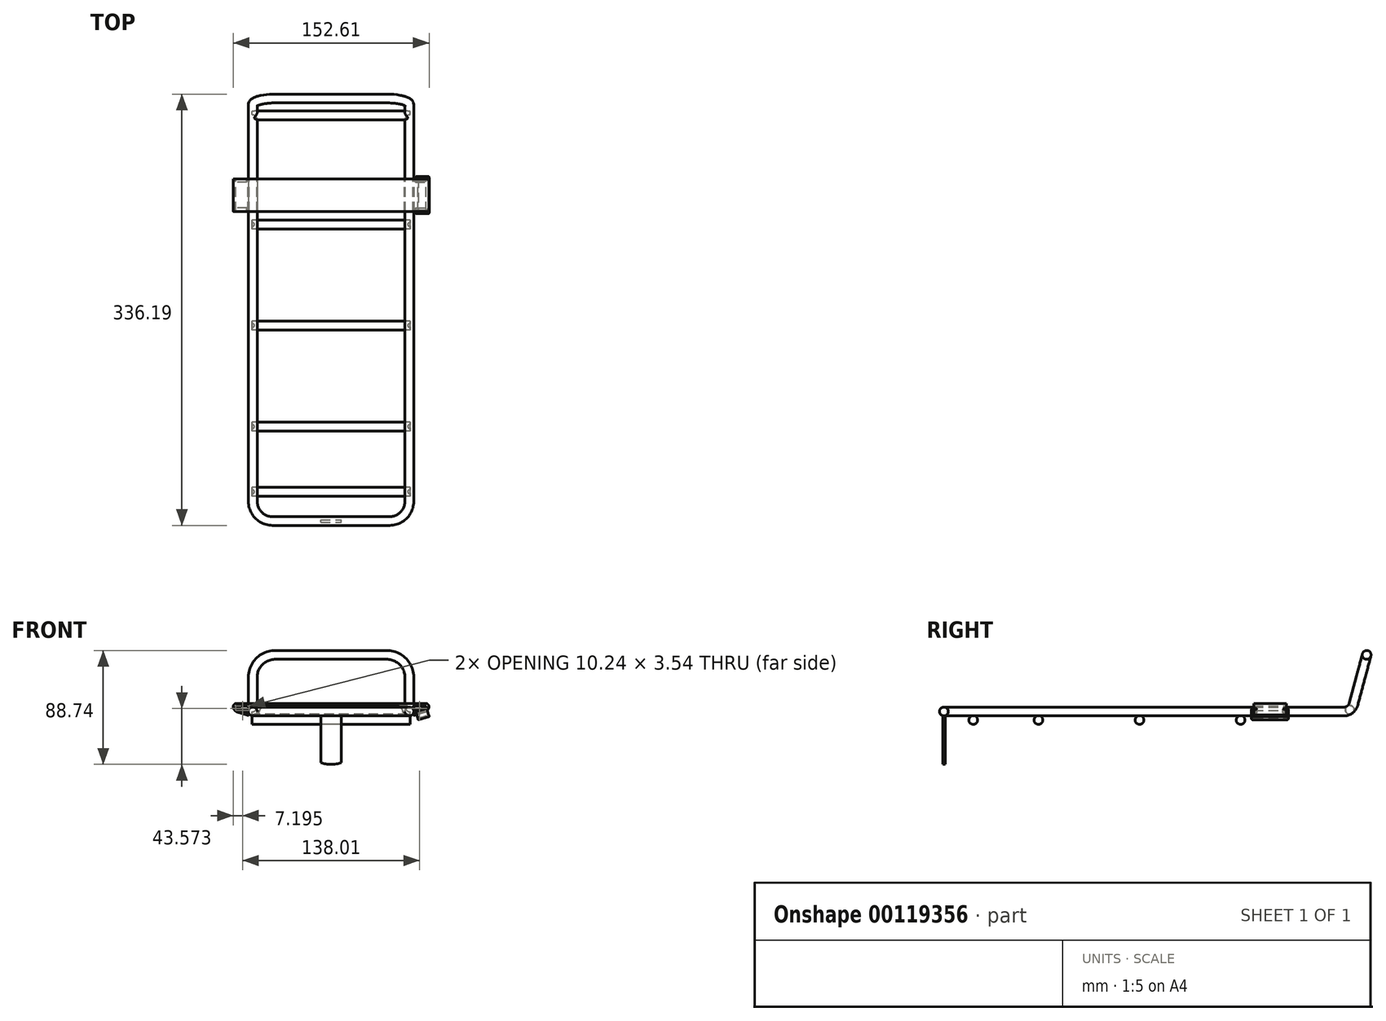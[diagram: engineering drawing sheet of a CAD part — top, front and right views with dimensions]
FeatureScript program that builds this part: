
annotation { "Feature Type Name" : "Feature", "Feature Type Description" : "" }
export const myFeature = defineFeature(function(context is Context, id is Id, definition is map)
    precondition{}
    {
        {
            var Q0;
            Q0=qCreatedBy(makeId("Right.planeOp"),FACE);
            var sketch = newSketch(context, id + "F0", { "sketchPlane" : qUnion([Q0])});
            skCircle(sketch, "E0", {"center": v(0, 0) * mm, "radius": 3.43 * mm});
            skSolve(sketch);
        }
        {
            var Q0;
            Q0=qCreatedBy(makeId("Top.planeOp"),FACE);
            var sketch = newSketch(context, id + "F1", { "sketchPlane" : qUnion([Q0])});
            skLineSegment(sketch, "E1", {"start": v(0, 0) * mm, "end": v(45.72, 0) * mm});
            skArc(sketch, "E2", {"start": v(45.72, 0) * mm, "mid": v(56.5, 4.46) * mm, "end": v(60.96, 15.24) * mm});
            skLineSegment(sketch, "E3", {"start": v(45.72, 0) * mm, "end": v(60.96, 0) * mm, "construction": true});
            skLineSegment(sketch, "E4", {"start": v(60.96, 0) * mm, "end": v(60.96, 15.24) * mm, "construction": true});
            skSolve(sketch);
        }
        {
            var Q0;
            Q0=sQuery(id+"F1.wireOp",EDGE,"E4");
            cPlane(context, id + "F2", {"entities" : qUnion([Q0]), "cplaneType" : CPlaneType.LINE_ANGLE, "offset" : 25.4 * mm, "angle" : 90 * degree, "width" : 152.4 * mm, "height" : 152.4 * mm});
        }
        {
            var Q0;
            Q0=qCreatedBy(id+"F2.planeOp",FACE);
            var sketch = newSketch(context, id + "F3", { "sketchPlane" : qUnion([Q0])});
            skLineSegment(sketch, "E5", {"start": v(15.24, 0) * mm, "end": v(311.65, 0) * mm});
            skArc(sketch, "E6", {"start": v(311.65, 0) * mm, "mid": v(316.3, 1.57) * mm, "end": v(319.01, 5.65) * mm});
            skLineSegment(sketch, "E7", {"start": v(311.65, 0) * mm, "end": v(317.5, 0) * mm, "construction": true});
            skLineSegment(sketch, "E8", {"start": v(317.5, 0) * mm, "end": v(319.01, 5.65) * mm, "construction": true});
            skSolve(sketch);
        }
        {
            var Q0;
            Q0=sQuery(id+"F3.wireOp",EDGE,"E8");
            cPlane(context, id + "F4", {"entities" : qUnion([Q0]), "cplaneType" : CPlaneType.LINE_ANGLE, "offset" : 25.4 * mm, "angle" : 90 * degree, "width" : 152.4 * mm, "height" : 152.4 * mm});
        }
        {
            var Q0;
            Q0=qCreatedBy(id+"F4.planeOp",FACE);
            var sketch = newSketch(context, id + "F5", { "sketchPlane" : qUnion([Q0])});
            skLineSegment(sketch, "E9", {"start": v(-60.96, 88.02) * mm, "end": v(-60.96, 110.12) * mm});
            skArc(sketch, "E10", {"start": v(-43.18, 127.9) * mm, "mid": v(-55.75, 122.69) * mm, "end": v(-60.96, 110.12) * mm});
            skLineSegment(sketch, "E11", {"start": v(-43.18, 127.9) * mm, "end": v(43.18, 127.9) * mm});
            skArc(sketch, "E12", {"start": v(60.96, 110.12) * mm, "mid": v(55.75, 122.69) * mm, "end": v(43.18, 127.9) * mm});
            skLineSegment(sketch, "E13", {"start": v(60.96, 110.12) * mm, "end": v(60.96, 88.02) * mm});
            skLineSegment(sketch, "E14", {"start": v(-60.96, 110.12) * mm, "end": v(-60.96, 127.9) * mm, "construction": true});
            skLineSegment(sketch, "E15", {"start": v(-60.96, 127.9) * mm, "end": v(-43.18, 127.9) * mm, "construction": true});
            skLineSegment(sketch, "E16", {"start": v(43.18, 127.9) * mm, "end": v(60.96, 127.9) * mm, "construction": true});
            skLineSegment(sketch, "E17", {"start": v(60.96, 127.9) * mm, "end": v(60.96, 110.12) * mm, "construction": true});
            skLineSegment(sketch, "E18", {"start": v(-60.96, 88.02) * mm, "end": v(60.96, 88.02) * mm, "construction": true});
            skLineSegment(sketch, "E19", {"start": v(0, 88.02) * mm, "end": v(0, 0) * mm, "construction": true});
            skSolve(sketch);
        }
        {
            var Q0;
            Q0=sQuery(id+"F5.wireOp",EDGE,"E13");
            cPlane(context, id + "F6", {"entities" : qUnion([Q0]), "cplaneType" : CPlaneType.LINE_ANGLE, "offset" : 25.4 * mm, "angle" : 0 * degree, "width" : 152.4 * mm, "height" : 152.4 * mm});
        }
        {
            var Q0;
            Q0=qCreatedBy(id+"F6.planeOp",FACE);
            var sketch = newSketch(context, id + "F7", { "sketchPlane" : qUnion([Q0])});
            skArc(sketch, "E20", {"start": v(-319.01, 5.65) * mm, "mid": v(-316.3, 1.57) * mm, "end": v(-311.65, 0) * mm});
            skLineSegment(sketch, "E21", {"start": v(-311.65, 0) * mm, "end": v(-15.24, 0) * mm});
            skSolve(sketch);
        }
        {
            var Q0;
            Q0=qCreatedBy(makeId("Top.planeOp"),FACE);
            var sketch = newSketch(context, id + "F8", { "sketchPlane" : qUnion([Q0])});
            skArc(sketch, "E22", {"start": v(-60.96, 15.24) * mm, "mid": v(-56.5, 4.46) * mm, "end": v(-45.72, 0) * mm});
            skLineSegment(sketch, "E23", {"start": v(-45.72, 0) * mm, "end": v(0, 0) * mm});
            skSolve(sketch);
        }
        {
            var Q0;
            Q0=qSketchRegion(id+"F0",true);
            var Q1;
            Q1=qConstructionFilter(qBodyType(qCreatedBy(id+"F1",EDGE),BodyType.WIRE),ConstructionObject.NO);
            var Q2;
            Q2=qConstructionFilter(qBodyType(qCreatedBy(id+"F3",EDGE),BodyType.WIRE),ConstructionObject.NO);
            var Q3;
            Q3=qConstructionFilter(qBodyType(qCreatedBy(id+"F5",EDGE),BodyType.WIRE),ConstructionObject.NO);
            var Q4;
            Q4=qConstructionFilter(qBodyType(qCreatedBy(id+"F7",EDGE),BodyType.WIRE),ConstructionObject.NO);
            var Q5;
            Q5=qConstructionFilter(qBodyType(qCreatedBy(id+"F8",EDGE),BodyType.WIRE),ConstructionObject.NO);
            sweep(context, id + "F9", {"profiles" : qUnion([Q0]), "path" : qUnion([Q1, Q2, Q3, Q4, Q5])});
        }
        {
            var Q0;
            Q0=qCreatedBy(makeId("Front.planeOp"),FACE);
            var sketch = newSketch(context, id + "F10", { "sketchPlane" : qUnion([Q0])});
            skLineSegment(sketch, "E24.bottom", {"start": v(-8, 0) * mm, "end": v(8, 0) * mm});
            skLineSegment(sketch, "E24.left", {"start": v(-8, 0) * mm, "end": v(-8, -39.85) * mm});
            skLineSegment(sketch, "E24.right", {"start": v(8, 0) * mm, "end": v(8, -39.85) * mm});
            skArc(sketch, "E25", {"start": v(-8, -39.85) * mm, "mid": v(0, -41.15) * mm, "end": v(8, -39.85) * mm});
            skSolve(sketch);
        }
        {
            var Q0;
            Q0=qSketchRegion(id+"F10",true);
            extrude(context, id + "F11", {"entities" : qUnion([Q0]), "operationType" : NewBodyOperationType.ADD, "endBound" : BoundingType.SYMMETRIC, "depth" : 2.03 * mm});
        }
        {
            var Q0;
            Q0=qCreatedBy(makeId("Right.planeOp"),FACE);
            var sketch = newSketch(context, id + "F12", { "sketchPlane" : qUnion([Q0])});
            skCircle(sketch, "E26", {"center": v(22.86, -6.6) * mm, "radius": 3.43 * mm});
            skCircle(sketch, "E27", {"center": v(73.66, -6.6) * mm, "radius": 3.43 * mm});
            skLineSegment(sketch, "E28", {"start": v(0, -3.18) * mm, "end": v(311.65, -3.18) * mm, "construction": true});
            skCircle(sketch, "E29", {"center": v(152.4, -6.6) * mm, "radius": 3.43 * mm});
            skCircle(sketch, "E30", {"center": v(231.14, -6.6) * mm, "radius": 3.43 * mm});
            skCircle(sketch, "E31", {"center": v(316.23, 1.27) * mm, "radius": 3.43 * mm});
            skSolve(sketch);
        }
        {
            var Q0;
            Q0=qSketchRegion(id+"F12",true);
            extrude(context, id + "F13", {"entities" : qUnion([Q0]), "operationType" : NewBodyOperationType.ADD, "endBound" : BoundingType.SYMMETRIC, "depth" : 123.19 * mm});
        }
        {
            var Q0;
            Q0=qCreatedBy(makeId("Front.planeOp"),FACE);
            cPlane(context, id + "F14", {"entities" : qUnion([Q0]), "cplaneType" : CPlaneType.OFFSET, "offset" : 266.7 * mm, "oppositeDirection" : true, "width" : 152.4 * mm, "height" : 152.4 * mm});
        }
        {
            var Q0;
            Q0=qCreatedBy(id+"F14.planeOp",FACE);
            var sketch = newSketch(context, id + "F15", { "sketchPlane" : qUnion([Q0])});
            skCircle(sketch, "E32", {"center": v(-60.96, 0) * mm, "radius": 3.43 * mm, "construction": true});
            skCircle(sketch, "E33", {"center": v(60.96, 0) * mm, "radius": 3.43 * mm, "construction": true});
            skLineSegment(sketch, "E34", {"start": v(60.96, 3.43) * mm, "end": v(-60.96, 3.43) * mm, "construction": true});
            skArc(sketch, "E35", {"start": v(73.91, 6.22) * mm, "mid": v(75.53, 5.55) * mm, "end": v(76.2, 3.94) * mm});
            skArc(sketch, "E36", {"start": v(76.2, 3.94) * mm, "mid": v(75.3, 1.22) * mm, "end": v(72.96, -0.44) * mm});
            skArc(sketch, "E37", {"start": v(-73.91, 6.22) * mm, "mid": v(-75.53, 5.55) * mm, "end": v(-76.2, 3.94) * mm});
            skArc(sketch, "E38", {"start": v(-76.2, 3.94) * mm, "mid": v(-75.3, 1.22) * mm, "end": v(-72.96, -0.44) * mm});
            skArc(sketch, "E39", {"start": v(64.2, -2.2) * mm, "mid": v(60.96, 3.43) * mm, "end": v(57.72, -2.2) * mm});
            skArc(sketch, "E40", {"start": v(64.2, -2.2) * mm, "mid": v(64.25, -2.76) * mm, "end": v(64.8, -2.93) * mm});
            skArc(sketch, "E41", {"start": v(57.72, -2.2) * mm, "mid": v(57.54, -2.88) * mm, "end": v(56.85, -2.73) * mm});
            skArc(sketch, "E42", {"start": v(-57.72, -2.2) * mm, "mid": v(-60.96, 3.43) * mm, "end": v(-64.2, -2.2) * mm});
            skArc(sketch, "E43", {"start": v(-57.72, -2.2) * mm, "mid": v(-57.54, -2.88) * mm, "end": v(-56.85, -2.73) * mm});
            skLineSegment(sketch, "E44", {"start": v(-72.96, -0.44) * mm, "end": v(-64.8, -2.93) * mm});
            skArc(sketch, "E45", {"start": v(-64.2, -2.2) * mm, "mid": v(-64.25, -2.76) * mm, "end": v(-64.8, -2.93) * mm});
            skLineSegment(sketch, "E46", {"start": v(64.8, -2.93) * mm, "end": v(72.96, -0.44) * mm});
            skLineSegment(sketch, "E47", {"start": v(73.91, 6.22) * mm, "end": v(0, 6.22) * mm});
            skLineSegment(sketch, "E48", {"start": v(0, 6.22) * mm, "end": v(-73.91, 6.22) * mm});
            skLineSegment(sketch, "E49", {"start": v(50.99, 4.2) * mm, "end": v(-50.99, 4.2) * mm});
            skArc(sketch, "E50", {"start": v(-56.85, -2.73) * mm, "mid": v(-56.3, -1.63) * mm, "end": v(-56.05, -0.44) * mm});
            skArc(sketch, "E51", {"start": v(56.05, -0.44) * mm, "mid": v(56.3, -1.63) * mm, "end": v(56.85, -2.73) * mm});
            skArc(sketch, "E52", {"start": v(56.05, -0.44) * mm, "mid": v(54.42, 2.86) * mm, "end": v(50.99, 4.2) * mm});
            skArc(sketch, "E53", {"start": v(-50.99, 4.2) * mm, "mid": v(-54.42, 2.86) * mm, "end": v(-56.05, -0.44) * mm});
            skLineSegment(sketch, "E54", {"start": v(64.64, -2.45) * mm, "end": v(57.28, -2.45) * mm, "construction": true});
            skLineSegment(sketch, "E55", {"start": v(-57.28, -2.45) * mm, "end": v(-64.64, -2.45) * mm, "construction": true});
            skSolve(sketch);
        }
        {
            var Q0;
            Q0=qSketchRegion(id+"F15",true);
            extrude(context, id + "F16", {"entities" : qUnion([Q0]), "depth" : 25.4 * mm});
        }
        {
            var Q0;
            Q0=makeQuery(id+"F16.opExtrude","CAP_FACE",FACE,{"disambiguationData":[OSD([sQuery(id+"F15.wireOp",EDGE,"E35"),sQuery(id+"F15.wireOp",EDGE,"E36"),sQuery(id+"F15.wireOp",EDGE,"E37"),sQuery(id+"F15.wireOp",EDGE,"E38"),sQuery(id+"F15.wireOp",EDGE,"E39"),sQuery(id+"F15.wireOp",EDGE,"E40"),sQuery(id+"F15.wireOp",EDGE,"E41"),sQuery(id+"F15.wireOp",EDGE,"E42"),sQuery(id+"F15.wireOp",EDGE,"E43"),sQuery(id+"F15.wireOp",EDGE,"E44"),sQuery(id+"F15.wireOp",EDGE,"E45"),sQuery(id+"F15.wireOp",EDGE,"E46"),sQuery(id+"F15.wireOp",EDGE,"E47"),sQuery(id+"F15.wireOp",EDGE,"E48"),sQuery(id+"F15.wireOp",EDGE,"E49"),sQuery(id+"F15.wireOp",EDGE,"E50"),sQuery(id+"F15.wireOp",EDGE,"E51"),sQuery(id+"F15.wireOp",EDGE,"E52"),sQuery(id+"F15.wireOp",EDGE,"E53")])],"isStart":true});
            var sketch = newSketch(context, id + "F17", { "sketchPlane" : qUnion([Q0])});
            skLineSegment(sketch, "E56", {"start": v(62.5, 4.2) * mm, "end": v(73.51, 4.2) * mm});
            skLineSegment(sketch, "E57", {"start": v(65.65, 0.52) * mm, "end": v(73.7, 2.97) * mm});
            skArc(sketch, "E58", {"start": v(73.51, 4.2) * mm, "mid": v(74.13, 3.66) * mm, "end": v(73.7, 2.97) * mm});
            skArc(sketch, "E59", {"start": v(65.65, 0.52) * mm, "mid": v(64.57, 2.78) * mm, "end": v(62.5, 4.2) * mm});
            skLineSegment(sketch, "E60", {"start": v(-73.51, 4.2) * mm, "end": v(-62.5, 4.2) * mm});
            skLineSegment(sketch, "E61", {"start": v(-65.65, 0.52) * mm, "end": v(-73.7, 2.97) * mm});
            skArc(sketch, "E62", {"start": v(-73.51, 4.2) * mm, "mid": v(-74.13, 3.66) * mm, "end": v(-73.7, 2.97) * mm});
            skArc(sketch, "E63", {"start": v(-62.5, 4.2) * mm, "mid": v(-64.57, 2.78) * mm, "end": v(-65.65, 0.52) * mm});
            skSolve(sketch);
        }
        {
            var Q0;
            Q0=qSketchRegion(id+"F17",true);
            extrude(context, id + "F18", {"entities" : qUnion([Q0]), "operationType" : NewBodyOperationType.REMOVE, "endBound" : BoundingType.UP_TO_NEXT, "oppositeDirection" : true, "depth" : 25.4 * mm});
        }
        {
            var Q0;
            Q0=makeQuery(id+"F16.opExtrude","SWEPT_EDGE",EDGE,{"disambiguationData":[OSD([sQuery(id+"F15.wireOp",EDGE,"E36"),sQuery(id+"F15.wireOp",EDGE,"E46")])]});
            var Q1;
            Q1=makeQuery(id+"F16.opExtrude","SWEPT_FACE",FACE,{"disambiguationData":[OSD([sQuery(id+"F15.wireOp",EDGE,"E46")])]});
            cPlane(context, id + "F19", {"entities" : qUnion([Q0, Q1]), "cplaneType" : CPlaneType.LINE_ANGLE, "offset" : 25.4 * mm, "angle" : 90 * degree, "width" : 152.4 * mm, "height" : 152.4 * mm});
        }
        {
            var Q0;
            Q0=qCreatedBy(id+"F19.planeOp",FACE);
            var sketch = newSketch(context, id + "F20", { "sketchPlane" : qUnion([Q0])});
            skLineSegment(sketch, "E64", {"start": v(241.3, -20.93) * mm, "end": v(241.3, -19.5) * mm});
            skLineSegment(sketch, "E65", {"start": v(241.3, -19.5) * mm, "end": v(243.95, -20.22) * mm});
            skLineSegment(sketch, "E66", {"start": v(243.95, -20.22) * mm, "end": v(241.3, -20.93) * mm});
            skLineSegment(sketch, "E67", {"start": v(241.3, -21.74) * mm, "end": v(241.3, -20.93) * mm, "construction": true});
            skLineSegment(sketch, "E68", {"start": v(266.7, -21.74) * mm, "end": v(266.7, -20.93) * mm, "construction": true});
            skLineSegment(sketch, "E69", {"start": v(266.7, -20.93) * mm, "end": v(266.7, -19.5) * mm});
            skLineSegment(sketch, "E70", {"start": v(266.7, -19.5) * mm, "end": v(264.05, -20.22) * mm});
            skLineSegment(sketch, "E71", {"start": v(264.05, -20.22) * mm, "end": v(266.7, -20.93) * mm});
            skSolve(sketch);
        }
        {
            var Q0;
            Q0=qSketchRegion(id+"F20",true);
            var Q1;
            Q1=makeQuery(id+"F18.boolean.opBoolean","COPY",FACE,{"derivedFrom":makeQuery(id+"F18.opExtrude","SWEPT_FACE",FACE,{"disambiguationData":[OSD([sQuery(id+"F17.wireOp",EDGE,"E63")])]})});
            var Q2;
            Q2=makeQuery(id+"F16.opExtrude","SWEPT_FACE",FACE,{"disambiguationData":[OSD([sQuery(id+"F15.wireOp",EDGE,"E36")])]});
            extrude(context, id + "F21", {"entities" : qUnion([Q0]), "operationType" : NewBodyOperationType.REMOVE, "endBound" : BoundingType.UP_TO_SURFACE, "oppositeDirection" : true, "endBoundEntityFace" : qUnion([Q1]), "depth" : 152.4 * mm, "hasSecondDirection" : true, "secondDirectionBound" : SecondDirectionBoundingType.UP_TO_SURFACE, "secondDirectionOppositeDirection" : false, "secondDirectionBoundEntityFace" : qUnion([Q2]), "secondDirectionDepth" : 25.4 * mm});
        }
        {
            var Q0;
            Q0=makeQuery(id+"F16.opExtrude","SWEPT_EDGE",EDGE,{"disambiguationData":[OSD([sQuery(id+"F15.wireOp",EDGE,"E38"),sQuery(id+"F15.wireOp",EDGE,"E44")])]});
            var Q1;
            Q1=makeQuery(id+"F16.opExtrude","SWEPT_FACE",FACE,{"disambiguationData":[OSD([sQuery(id+"F15.wireOp",EDGE,"E44")])]});
            cPlane(context, id + "F22", {"entities" : qUnion([Q0, Q1]), "cplaneType" : CPlaneType.LINE_ANGLE, "offset" : 25.4 * mm, "angle" : 90 * degree, "width" : 152.4 * mm, "height" : 152.4 * mm});
        }
        {
            var Q0;
            Q0=qCreatedBy(id+"F22.planeOp",FACE);
            var sketch = newSketch(context, id + "F23", { "sketchPlane" : qUnion([Q0])});
            skLineSegment(sketch, "E72", {"start": v(266.7, -19.5) * mm, "end": v(264.05, -20.22) * mm});
            skLineSegment(sketch, "E73", {"start": v(266.7, -19.5) * mm, "end": v(266.7, -20.93) * mm});
            skLineSegment(sketch, "E74", {"start": v(266.7, -20.93) * mm, "end": v(264.05, -20.22) * mm});
            skLineSegment(sketch, "E75", {"start": v(266.7, -20.93) * mm, "end": v(266.7, -21.74) * mm, "construction": true});
            skLineSegment(sketch, "E76", {"start": v(241.3, -21.74) * mm, "end": v(241.3, -20.93) * mm, "construction": true});
            skLineSegment(sketch, "E77", {"start": v(241.3, -20.93) * mm, "end": v(241.3, -19.5) * mm});
            skLineSegment(sketch, "E78", {"start": v(241.3, -19.5) * mm, "end": v(243.95, -20.22) * mm});
            skLineSegment(sketch, "E79", {"start": v(243.95, -20.22) * mm, "end": v(241.3, -20.93) * mm});
            skSolve(sketch);
        }
        {
            var Q0;
            Q0=qSketchRegion(id+"F23",true);
            var Q1;
            Q1=makeQuery(id+"F18.boolean.opBoolean","COPY",FACE,{"derivedFrom":makeQuery(id+"F18.opExtrude","SWEPT_FACE",FACE,{"disambiguationData":[OSD([sQuery(id+"F17.wireOp",EDGE,"E59")])]})});
            var Q2;
            Q2=makeQuery(id+"F16.opExtrude","SWEPT_FACE",FACE,{"disambiguationData":[OSD([sQuery(id+"F15.wireOp",EDGE,"E38")])]});
            extrude(context, id + "F24", {"entities" : qUnion([Q0]), "operationType" : NewBodyOperationType.REMOVE, "endBound" : BoundingType.UP_TO_SURFACE, "endBoundEntityFace" : qUnion([Q1]), "depth" : 152.4 * mm, "hasSecondDirection" : true, "secondDirectionBound" : SecondDirectionBoundingType.UP_TO_SURFACE, "secondDirectionOppositeDirection" : true, "secondDirectionBoundEntityFace" : qUnion([Q2]), "secondDirectionDepth" : 25.4 * mm});
        }
        {
            var Q0;
            Q0=qCreatedBy(id+"F19.planeOp",FACE);
            var sketch = newSketch(context, id + "F25", { "sketchPlane" : qUnion([Q0])});
            skLineSegment(sketch, "E80", {"start": v(239.52, -19.1) * mm, "end": v(243.66, -20.22) * mm});
            skLineSegment(sketch, "E81", {"start": v(243.66, -20.22) * mm, "end": v(240.8, -20.99) * mm});
            skLineSegment(sketch, "E82", {"start": v(240.8, -20.99) * mm, "end": v(240.8, -24.8) * mm});
            skLineSegment(sketch, "E83", {"start": v(267.2, -24.8) * mm, "end": v(267.2, -20.99) * mm});
            skLineSegment(sketch, "E84", {"start": v(267.2, -20.99) * mm, "end": v(264.34, -20.22) * mm});
            skLineSegment(sketch, "E85", {"start": v(264.34, -20.22) * mm, "end": v(268.48, -19.1) * mm});
            skLineSegment(sketch, "E86", {"start": v(268.48, -19.1) * mm, "end": v(268.48, -26.06) * mm});
            skLineSegment(sketch, "E87", {"start": v(268.48, -26.06) * mm, "end": v(239.52, -26.06) * mm});
            skLineSegment(sketch, "E88", {"start": v(239.52, -26.06) * mm, "end": v(239.52, -19.1) * mm});
            skLineSegment(sketch, "E89.top", {"start": v(240.8, -24.8) * mm, "end": v(267.2, -24.8) * mm});
            skLineSegment(sketch, "E90", {"start": v(254, -24.8) * mm, "end": v(254, -26.06) * mm, "construction": true});
            skLineSegment(sketch, "E91", {"start": v(266.7, -21.34) * mm, "end": v(267.2, -21.34) * mm, "construction": true});
            skLineSegment(sketch, "E92", {"start": v(240.8, -21.34) * mm, "end": v(241.3, -21.34) * mm, "construction": true});
            skLineSegment(sketch, "E93", {"start": v(267.2, -22.89) * mm, "end": v(268.48, -22.89) * mm, "construction": true});
            skLineSegment(sketch, "E94", {"start": v(241.6, -19.66) * mm, "end": v(241.61, -19.6) * mm, "construction": true});
            skLineSegment(sketch, "E95", {"start": v(242.23, -20.6) * mm, "end": v(242.25, -20.68) * mm, "construction": true});
            skLineSegment(sketch, "E96", {"start": v(265.77, -20.6) * mm, "end": v(265.75, -20.68) * mm, "construction": true});
            skLineSegment(sketch, "E97", {"start": v(266.4, -19.66) * mm, "end": v(266.39, -19.6) * mm, "construction": true});
            skSolve(sketch);
        }
        {
            var Q0;
            Q0=qSketchRegion(id+"F25",true);
            extrude(context, id + "F26", {"entities" : qUnion([Q0]), "oppositeDirection" : true, "depth" : 6.6 * mm, "hasSecondDirection" : true, "secondDirectionOppositeDirection" : false, "secondDirectionDepth" : 2.3 * mm});
        }
        {
            var Q0;
            Q0=makeQuery(id+"F26.opExtrude","SWEPT_EDGE",EDGE,{"disambiguationData":[OSD([sQuery(id+"F25.wireOp",EDGE,"E80"),sQuery(id+"F25.wireOp",EDGE,"E81")])]});
            var Q1;
            Q1=makeQuery(id+"F26.opExtrude","SWEPT_EDGE",EDGE,{"disambiguationData":[OSD([sQuery(id+"F25.wireOp",EDGE,"E84"),sQuery(id+"F25.wireOp",EDGE,"E85")])]});
            fillet(context, id + "F27", {"entities" : qUnion([Q0, Q1]), "radius" : 0.4 * mm, "tangentPropagation" : true, "allowEdgeOverflow" : false});
        }
        {
            var Q0;
            Q0=makeQuery(id+"F26.opExtrude","SWEPT_EDGE",EDGE,{"disambiguationData":[OSD([sQuery(id+"F25.wireOp",EDGE,"E81"),sQuery(id+"F25.wireOp",EDGE,"E82")])]});
            var Q1;
            Q1=makeQuery(id+"F26.opExtrude","SWEPT_EDGE",EDGE,{"disambiguationData":[OSD([sQuery(id+"F25.wireOp",EDGE,"E82"),sQuery(id+"F25.wireOp",EDGE,"E89.top")])]});
            var Q2;
            Q2=makeQuery(id+"F26.opExtrude","SWEPT_EDGE",EDGE,{"disambiguationData":[OSD([sQuery(id+"F25.wireOp",EDGE,"E83"),sQuery(id+"F25.wireOp",EDGE,"E89.top")])]});
            var Q3;
            Q3=makeQuery(id+"F26.opExtrude","SWEPT_EDGE",EDGE,{"disambiguationData":[OSD([sQuery(id+"F25.wireOp",EDGE,"E83"),sQuery(id+"F25.wireOp",EDGE,"E84")])]});
            fillet(context, id + "F28", {"entities" : qUnion([Q0, Q1, Q2, Q3]), "radius" : 0.5 * mm, "tangentPropagation" : true, "allowEdgeOverflow" : false});
        }
        {
            var Q0;
            Q0=makeQuery(id+"F26.opExtrude","SWEPT_EDGE",EDGE,{"disambiguationData":[OSD([sQuery(id+"F25.wireOp",EDGE,"E85"),sQuery(id+"F25.wireOp",EDGE,"E86")])]});
            var Q1;
            Q1=makeQuery(id+"F26.opExtrude","SWEPT_EDGE",EDGE,{"disambiguationData":[OSD([sQuery(id+"F25.wireOp",EDGE,"E86"),sQuery(id+"F25.wireOp",EDGE,"E87")])]});
            var Q2;
            Q2=makeQuery(id+"F26.opExtrude","SWEPT_EDGE",EDGE,{"disambiguationData":[OSD([sQuery(id+"F25.wireOp",EDGE,"E87"),sQuery(id+"F25.wireOp",EDGE,"E88")])]});
            var Q3;
            Q3=makeQuery(id+"F26.opExtrude","SWEPT_EDGE",EDGE,{"disambiguationData":[OSD([sQuery(id+"F25.wireOp",EDGE,"E80"),sQuery(id+"F25.wireOp",EDGE,"E88")])]});
            fillet(context, id + "F29", {"entities" : qUnion([Q0, Q1, Q2, Q3]), "radius" : 1.27 * mm, "tangentPropagation" : true, "allowEdgeOverflow" : false});
        }
        {
            var Q0;
            Q0=makeQuery(id+"F18.boolean.opBoolean","COPY",EDGE,{"derivedFrom":makeQuery(id+"F18.opExtrude","SWEPT_EDGE",EDGE,{"disambiguationData":[OSD([sQuery(id+"F17.wireOp",EDGE,"E57"),sQuery(id+"F17.wireOp",EDGE,"E59")])]})});
            var Q1;
            Q1=makeQuery(id+"F18.boolean.opBoolean","COPY",EDGE,{"derivedFrom":makeQuery(id+"F18.opExtrude","SWEPT_EDGE",EDGE,{"disambiguationData":[OSD([sQuery(id+"F17.wireOp",EDGE,"E56"),sQuery(id+"F17.wireOp",EDGE,"E59")])]})});
            var Q2;
            Q2=makeQuery(id+"F18.boolean.opBoolean","COPY",EDGE,{"derivedFrom":makeQuery(id+"F18.opExtrude","SWEPT_EDGE",EDGE,{"disambiguationData":[OSD([sQuery(id+"F17.wireOp",EDGE,"E60"),sQuery(id+"F17.wireOp",EDGE,"E63")])]})});
            var Q3;
            Q3=makeQuery(id+"F18.boolean.opBoolean","COPY",EDGE,{"derivedFrom":makeQuery(id+"F18.opExtrude","SWEPT_EDGE",EDGE,{"disambiguationData":[OSD([sQuery(id+"F17.wireOp",EDGE,"E61"),sQuery(id+"F17.wireOp",EDGE,"E63")])]})});
            fillet(context, id + "F30", {"entities" : qUnion([Q0, Q1, Q2, Q3]), "radius" : 0.5 * mm, "tangentPropagation" : true, "allowEdgeOverflow" : false});
        }
    });
